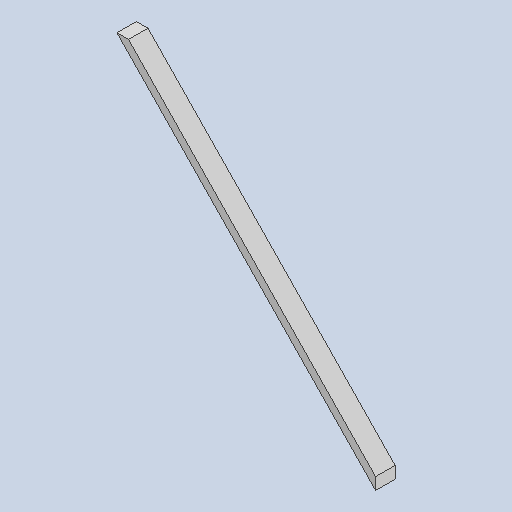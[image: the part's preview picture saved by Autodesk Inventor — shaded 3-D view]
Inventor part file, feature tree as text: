
AUTODESK INVENTOR PART (.ipt)
format: ipt  version: 2025 (Build 290162000, 162)  size: 139,776 bytes
history: native  units: in
note: dims shown in document units (in); Inventor stores cm internally (conversion verified against a paired STEP export)
features: other x4, reference x2, extrude x1, sketch x1
ambient origin geometry x8: Origin, YZ Plane, XZ Plane, XY Plane, X Axis, Y Axis, Z Axis, Center Point
bodies: Solid1 (feature_tree)
feature tree (8):
  extrude  "Extrusion1"  Depth=3.5in TaperAngle=0.0deg
  sketch  "Sketch1"  dims[d0=1.5in d1=3.5in d2=0.0in]
  reference  "Reference1"
  reference  "Reference2"
  other  "<userpath>\Documents\Tburn24\F_Legs2\F_Legs2.iam"
  other  "F_Legs2.iam"
  other  "4x2x4:5"
  other  "8'x2x4:3"
